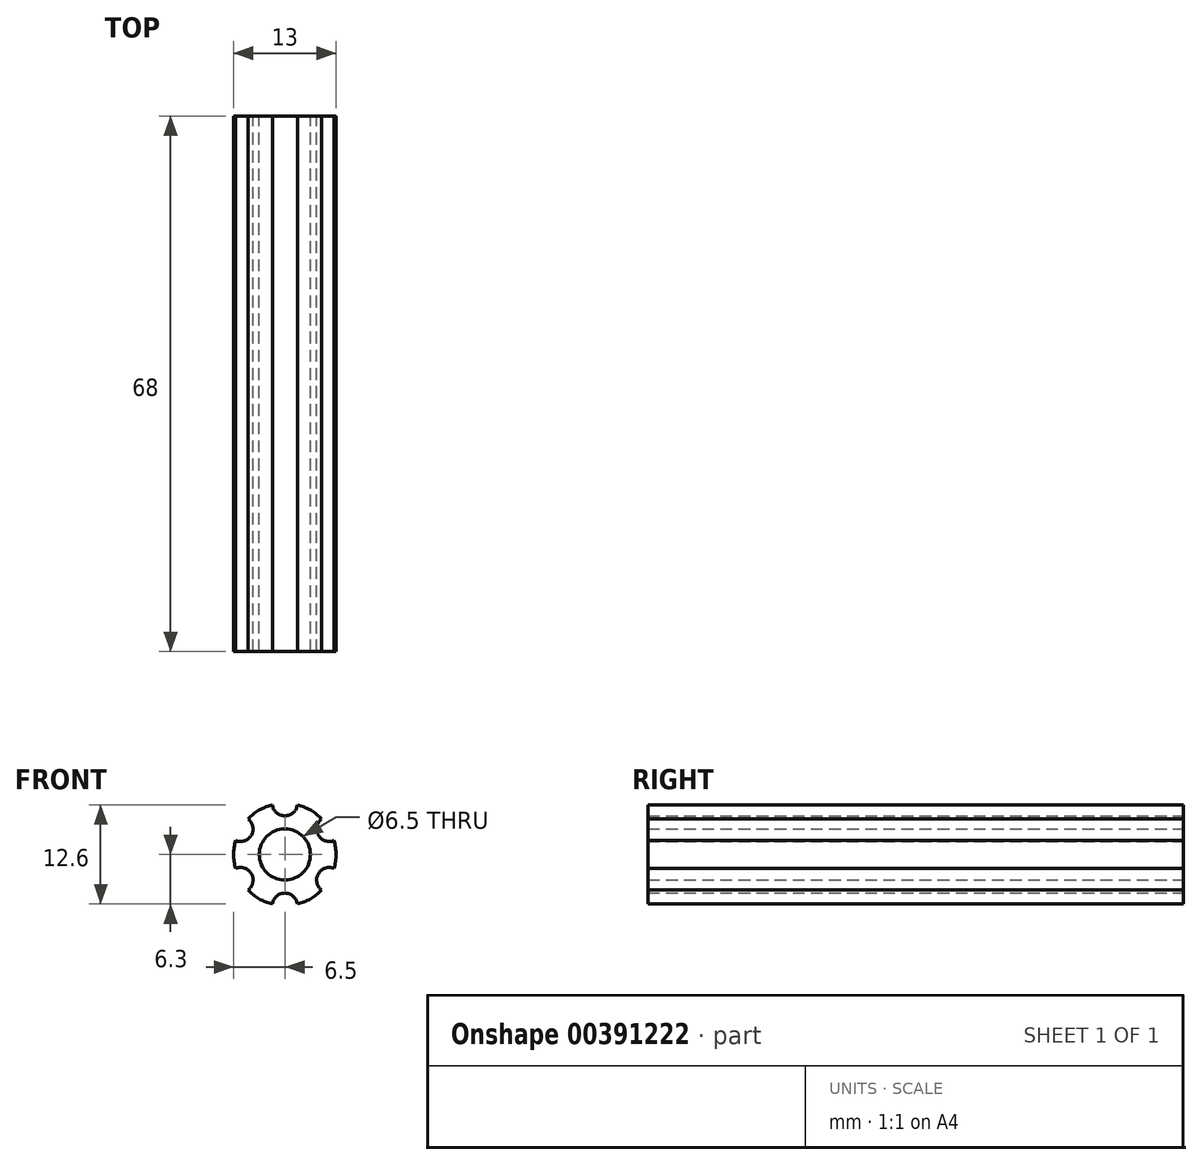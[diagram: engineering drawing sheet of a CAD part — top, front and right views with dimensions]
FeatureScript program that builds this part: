
annotation { "Feature Type Name" : "Feature", "Feature Type Description" : "" }
export const myFeature = defineFeature(function(context is Context, id is Id, definition is map)
    precondition{}
    {
        {
            var Q0;
            Q0=qCreatedBy(makeId("Front.planeOp"),FACE);
            var sketch = newSketch(context, id + "F0", { "sketchPlane" : qUnion([Q0])});
            skCircle(sketch, "E0", {"center": v(0, 0) * mm, "radius": 6.5 * mm});
            skCircle(sketch, "E1", {"center": v(0, 0) * mm, "radius": 3.25 * mm});
            skCircle(sketch, "E2.cCircle", {"center": v(0, 0) * mm, "radius": 5.64 * mm, "construction": true});
            skPoint(sketch, "E2.0.midPoint", {"position": v(2.82, -4.88) * mm});
            skCircle(sketch, "E3", {"center": v(0, 6.5) * mm, "radius": 1.6 * mm});
            skCircle(sketch, "E4", {"center": v(5.64, 3.25) * mm, "radius": 1.6 * mm});
            skCircle(sketch, "E5", {"center": v(5.64, -3.25) * mm, "radius": 1.6 * mm});
            skCircle(sketch, "E6", {"center": v(0, -6.5) * mm, "radius": 1.6 * mm});
            skCircle(sketch, "E7", {"center": v(-5.64, -3.25) * mm, "radius": 1.6 * mm});
            skCircle(sketch, "E8", {"center": v(-5.64, 3.25) * mm, "radius": 1.6 * mm});
            skSolve(sketch);
        }
        {
            var Q0;
            Q0=makeQuery(id+"F0.imprint","IMPRINT",FACE,{"disambiguationData":[TD([[makeQuery(id+"F0.imprint","IMPRINT",EDGE,{"derivedFrom":sQuery(id+"F0.wireOp",EDGE,"E1")}),-1.0]])]});
            extrude(context, id + "F1", {"entities" : qUnion([Q0]), "depth" : 68 * mm});
        }
    });
